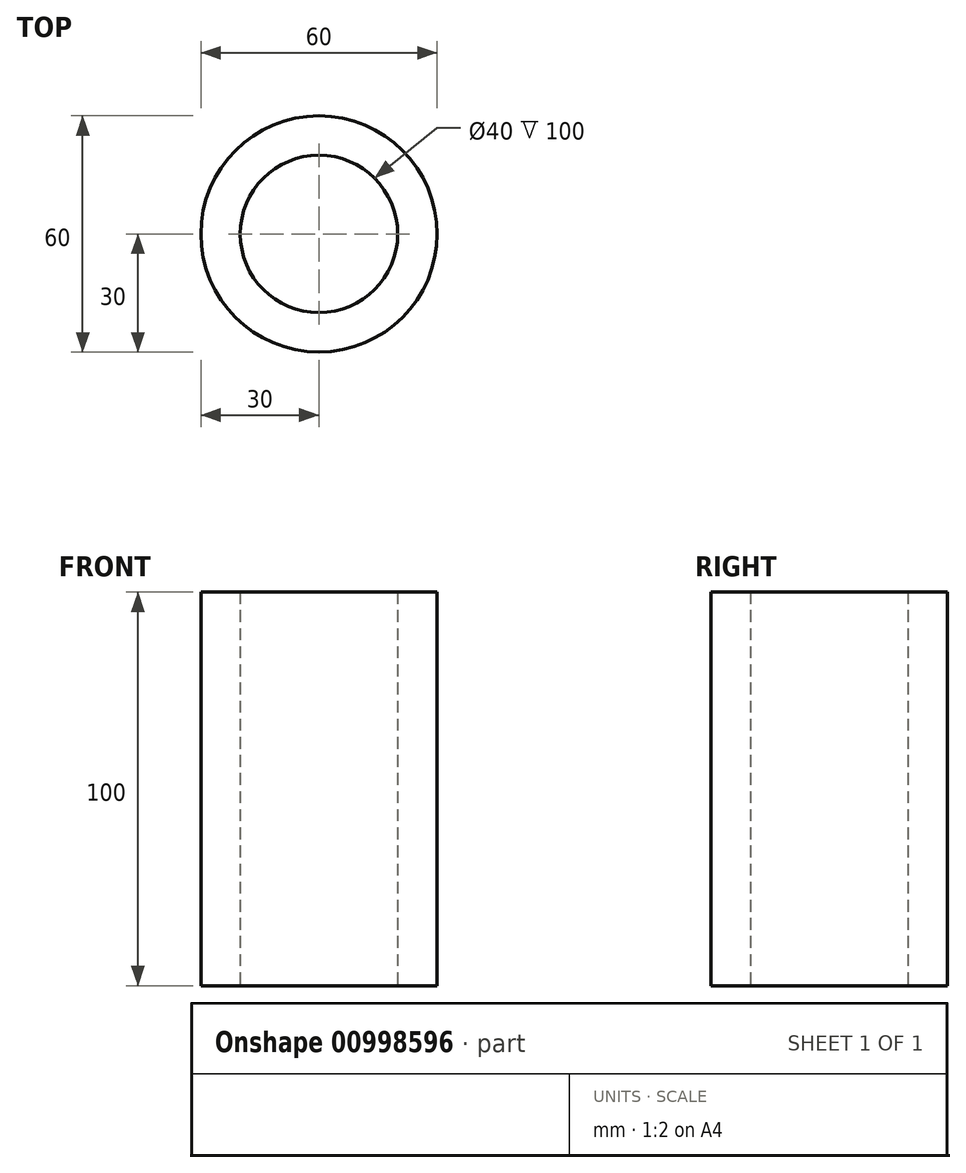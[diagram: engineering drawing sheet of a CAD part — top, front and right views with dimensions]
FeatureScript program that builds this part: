
annotation { "Feature Type Name" : "Feature", "Feature Type Description" : "" }
export const myFeature = defineFeature(function(context is Context, id is Id, definition is map)
    precondition{}
    {
        {
            var Q0;
            Q0=qCreatedBy(makeId("Top.planeOp"),FACE);
            var sketch = newSketch(context, id + "F0", { "sketchPlane" : qUnion([Q0])});
            skCircle(sketch, "E0", {"center": v(0, 0) * mm, "radius": 20 * mm});
            skCircle(sketch, "E1", {"center": v(0, 0) * mm, "radius": 30 * mm});
            skSolve(sketch);
        }
        {
            var Q0;
            Q0 = qSketchRegion(id + "F0", true);
            extrude(context, id + "F1", {"entities" : qUnion([Q0]), "depth" : 100 * mm, "offsetDistance" : 25 * mm});
        }
    });
